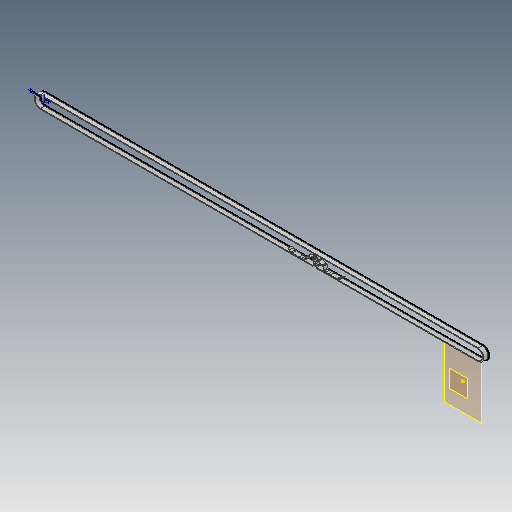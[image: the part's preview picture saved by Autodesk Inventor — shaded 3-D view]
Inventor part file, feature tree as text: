
AUTODESK INVENTOR PART (.ipt)
format: ipt  version: 2017 (Build 210142000, 142)  size: 212,480 bytes
history: native  units: mm
features: other x3, plane x2, sketch x2, extrude x1
ambient origin geometry x8: Origin, YZ Plane, XZ Plane, XY Plane, X Axis, Y Axis, Z Axis, Center Point
bodies: Body1 (feature_tree)
feature tree (8):
  plane  "Work Plane1"
  sketch  "Sketch1"  dims[d0=1.0mm d3=5.0mm d4=0.0mm]
  plane  "Work Plane2"
  extrude  "Extrusion2"  Depth=5.0mm TaperAngle=0.0deg
  sketch  "Sketch2"
  other  "<userpath>\OneDrive\SL-Inventor\SL-Beast 3D Printer\x-aXIS-aSSEMBLY.iam"
  other  "x-aXIS-aSSEMBLY.iam"
  other  "Z Motor Mount LC:1"
